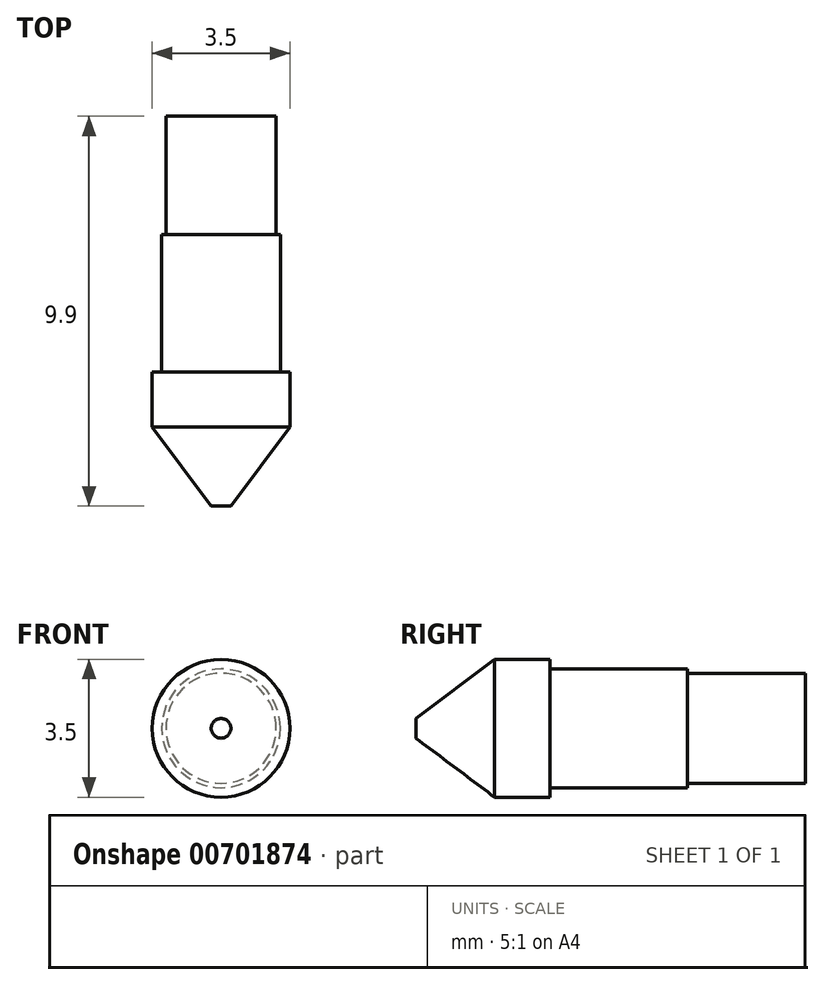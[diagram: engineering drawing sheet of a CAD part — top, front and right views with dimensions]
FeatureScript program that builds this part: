
annotation { "Feature Type Name" : "Feature", "Feature Type Description" : "" }
export const myFeature = defineFeature(function(context is Context, id is Id, definition is map)
    precondition{}
    {
        {
            var Q0;
            Q0=qCreatedBy(makeId("Front.planeOp"),FACE);
            var sketch = newSketch(context, id + "F0", { "sketchPlane" : qUnion([Q0])});
            skCircle(sketch, "E0", {"center": v(0, 0) * mm, "radius": 1.4 * mm});
            skSolve(sketch);
        }
        {
            var Q0;
            Q0=makeQuery(id+"F0.imprint","IMPRINT",FACE,{"disambiguationData":[TD([[makeQuery(id+"F0.imprint","IMPRINT",EDGE,{"derivedFrom":sQuery(id+"F0.wireOp",EDGE,"E0")}),1.0]])]});
            extrude(context, id + "F1", {"entities" : qUnion([Q0]), "depth" : 3 * mm, "offsetDistance" : 25 * mm});
        }
        {
            var Q0;
            Q0=makeQuery(id+"F1.opExtrude","CAP_FACE",FACE,{"disambiguationData":[OSD([sQuery(id+"F0.wireOp",EDGE,"E0")])],"isStart":false});
            var sketch = newSketch(context, id + "F2", { "sketchPlane" : qUnion([Q0])});
            skCircle(sketch, "E1", {"center": v(0, 0) * mm, "radius": 1.5 * mm});
            skSolve(sketch);
        }
        {
            var Q0;
            Q0=makeQuery(id+"F2.imprint","IMPRINT",FACE,{"disambiguationData":[TD([[makeQuery(id+"F2.imprint","IMPRINT",EDGE,{"derivedFrom":makeQuery(id+"F1.opExtrude","CAP_EDGE",EDGE,{"disambiguationData":[OSD([sQuery(id+"F0.wireOp",EDGE,"E0")])],"isStart":false})}),1.0]])]});
            var Q1;
            Q1=makeQuery(id+"F2.imprint","IMPRINT",FACE,{"disambiguationData":[TD([[makeQuery(id+"F2.imprint","IMPRINT",EDGE,{"derivedFrom":sQuery(id+"F2.wireOp",EDGE,"E1")}),1.0]])]});
            extrude(context, id + "F3", {"entities" : qUnion([Q0, Q1]), "depth" : 3.5 * mm, "offsetDistance" : 25 * mm});
        }
        {
            var Q0;
            Q0=makeQuery(id+"F3.opExtrude","CAP_FACE",FACE,{"disambiguationData":[OSD([sQuery(id+"F2.wireOp",EDGE,"E1")])],"isStart":false});
            var sketch = newSketch(context, id + "F4", { "sketchPlane" : qUnion([Q0])});
            skCircle(sketch, "E2", {"center": v(0, 0) * mm, "radius": 1.75 * mm});
            skSolve(sketch);
        }
        {
            var Q0;
            Q0=makeQuery(id+"F4.imprint","IMPRINT",FACE,{"disambiguationData":[TD([[makeQuery(id+"F4.imprint","IMPRINT",EDGE,{"derivedFrom":sQuery(id+"F4.wireOp",EDGE,"E2")}),1.0]])]});
            var Q1;
            Q1=makeQuery(id+"F4.imprint","IMPRINT",FACE,{"disambiguationData":[TD([[makeQuery(id+"F4.imprint","IMPRINT",EDGE,{"derivedFrom":makeQuery(id+"F3.opExtrude","CAP_EDGE",EDGE,{"disambiguationData":[OSD([sQuery(id+"F2.wireOp",EDGE,"E1")])],"isStart":false})}),1.0]])]});
            extrude(context, id + "F5", {"entities" : qUnion([Q0, Q1]), "depth" : 3.4 * mm, "offsetDistance" : 25 * mm});
        }
        {
            var Q0;
            Q0=makeQuery(id+"F5.opExtrude","CAP_EDGE",EDGE,{"disambiguationData":[OSD([sQuery(id+"F4.wireOp",EDGE,"E2")])],"isStart":false});
            chamfer(context, id + "F6", {"entities" : qUnion([Q0]), "chamferType" : ChamferType.TWO_OFFSETS, "width1" : 1.5 * mm, "oppositeDirection" : false, "width2" : 2 * mm, "tangentPropagation" : true});
        }
    });
